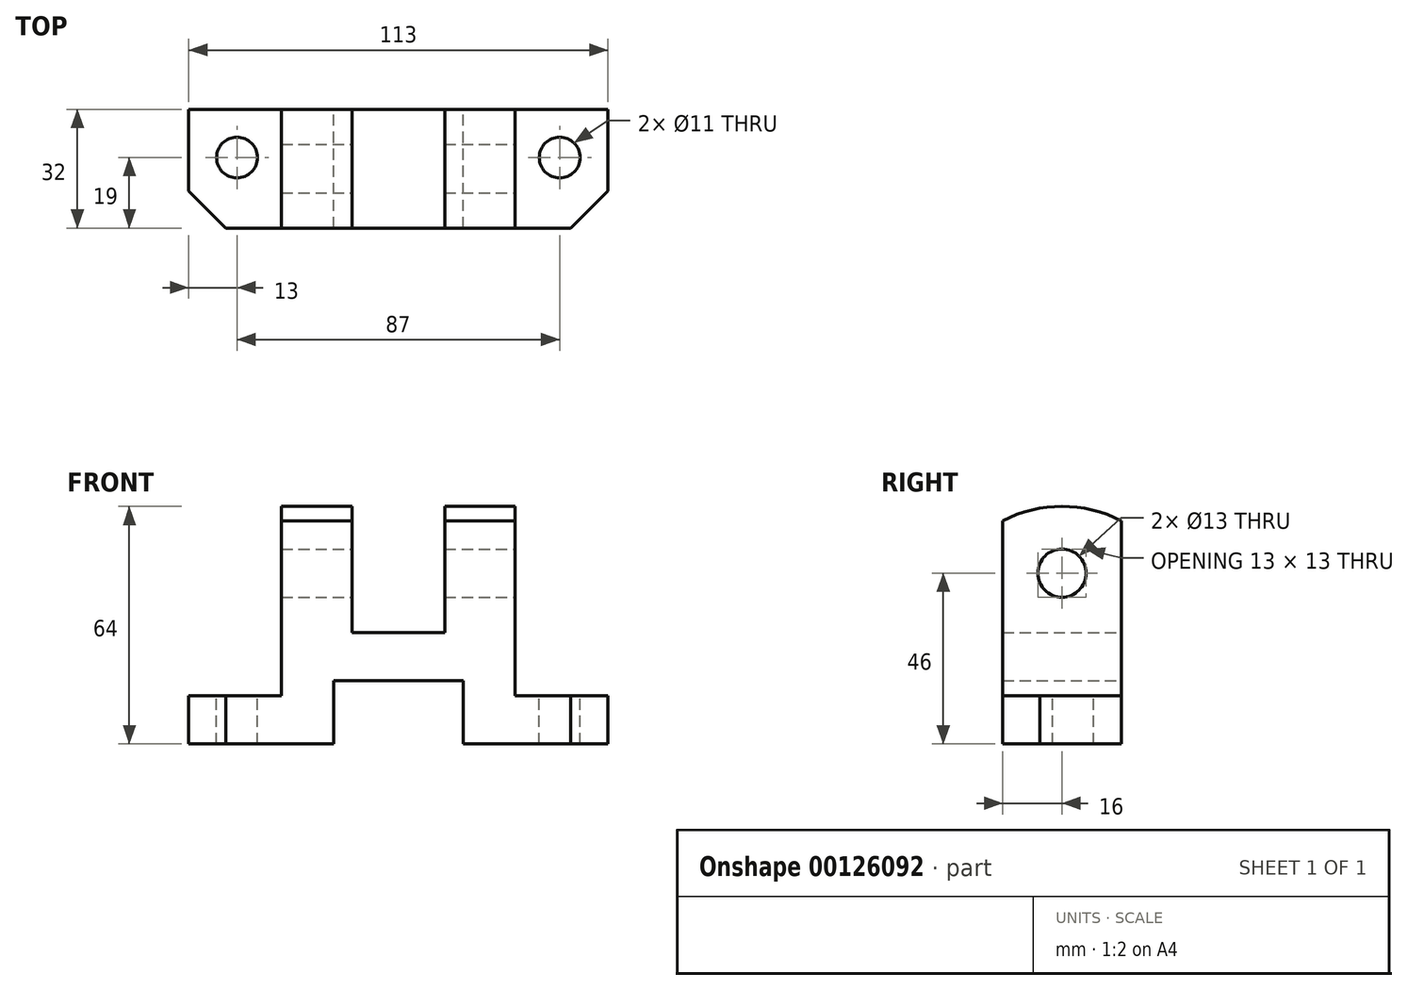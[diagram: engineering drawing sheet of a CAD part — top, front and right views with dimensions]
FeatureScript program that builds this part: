
annotation { "Feature Type Name" : "Feature", "Feature Type Description" : "" }
export const myFeature = defineFeature(function(context is Context, id is Id, definition is map)
    precondition{}
    {
        {
            var Q0;
            Q0=qCreatedBy(makeId("Front.planeOp"),FACE);
            var sketch = newSketch(context, id + "F0", { "sketchPlane" : qUnion([Q0])});
            skLineSegment(sketch, "E0", {"start": v(0, 0) * mm, "end": v(0, 17) * mm, "construction": true});
            skLineSegment(sketch, "E1", {"start": v(0, 17) * mm, "end": v(0, 30) * mm});
            skLineSegment(sketch, "E2", {"start": v(0, 30) * mm, "end": v(12.5, 30) * mm});
            skLineSegment(sketch, "E3", {"start": v(12.5, 30) * mm, "end": v(12.5, 64) * mm});
            skLineSegment(sketch, "E4", {"start": v(12.5, 64) * mm, "end": v(31.5, 64) * mm});
            skLineSegment(sketch, "E5", {"start": v(31.5, 64) * mm, "end": v(31.5, 13) * mm});
            skLineSegment(sketch, "E6", {"start": v(31.5, 13) * mm, "end": v(56.5, 13) * mm});
            skLineSegment(sketch, "E7", {"start": v(56.5, 13) * mm, "end": v(56.5, 0) * mm});
            skLineSegment(sketch, "E8", {"start": v(0, 17) * mm, "end": v(17.5, 17) * mm});
            skLineSegment(sketch, "E9", {"start": v(17.5, 17) * mm, "end": v(17.5, 0) * mm});
            skLineSegment(sketch, "E10", {"start": v(17.5, 0) * mm, "end": v(56.5, 0) * mm});
            skLineSegment(sketch, "E11.MirrorCS", {"start": v(-31.5, 64) * mm, "end": v(-31.5, 13) * mm});
            skLineSegment(sketch, "E12.MirrorCS", {"start": v(-12.5, 30) * mm, "end": v(-12.5, 64) * mm});
            skLineSegment(sketch, "E13.MirrorCS", {"start": v(0, 30) * mm, "end": v(-12.5, 30) * mm});
            skLineSegment(sketch, "E14.MirrorCS", {"start": v(0, 17) * mm, "end": v(-17.5, 17) * mm});
            skLineSegment(sketch, "E15.MirrorCS", {"start": v(-12.5, 64) * mm, "end": v(-31.5, 64) * mm});
            skLineSegment(sketch, "E16.MirrorCS", {"start": v(-17.5, 0) * mm, "end": v(-56.5, 0) * mm});
            skLineSegment(sketch, "E17.MirrorCS", {"start": v(-31.5, 13) * mm, "end": v(-56.5, 13) * mm});
            skLineSegment(sketch, "E18.MirrorCS", {"start": v(-56.5, 13) * mm, "end": v(-56.5, 0) * mm});
            skLineSegment(sketch, "E19", {"start": v(-17.5, 17) * mm, "end": v(-17.5, 0) * mm});
            skSolve(sketch);
        }
        {
            var Q0;
            Q0=makeQuery(id+"F0.imprint","IMPRINT",FACE,{"disambiguationData":[TD([[makeQuery(id+"F0.imprint","IMPRINT",EDGE,{"derivedFrom":sQuery(id+"F0.wireOp",EDGE,"E1")}),1.0]])]});
            var Q1;
            Q1=makeQuery(id+"F0.imprint","IMPRINT",FACE,{"disambiguationData":[TD([[makeQuery(id+"F0.imprint","IMPRINT",EDGE,{"derivedFrom":sQuery(id+"F0.wireOp",EDGE,"E1")}),-1.0]])]});
            extrude(context, id + "F1", {"entities" : qUnion([Q0, Q1]), "endBound" : BoundingType.SYMMETRIC, "depth" : 32 * mm});
        }
        {
            var Q0;
            Q0=makeQuery(id+"F1.opExtrude","CAP_EDGE",EDGE,{"disambiguationData":[OSD([sQuery(id+"F0.wireOp",EDGE,"E18.MirrorCS")])],"isStart":false});
            var Q1;
            Q1=makeQuery(id+"F1.opExtrude","CAP_EDGE",EDGE,{"disambiguationData":[OSD([sQuery(id+"F0.wireOp",EDGE,"E7")])],"isStart":false});
            chamfer(context, id + "F2", {"entities" : qUnion([Q0, Q1]), "width" : 10 * mm, "tangentPropagation" : true});
        }
        {
            var Q0;
            Q0=makeQuery(id+"F1.opExtrude","SWEPT_FACE",FACE,{"disambiguationData":[OSD([sQuery(id+"F0.wireOp",EDGE,"E6")])]});
            var sketch = newSketch(context, id + "F3", { "sketchPlane" : qUnion([Q0])});
            skLineSegment(sketch, "E20.bottom", {"start": v(56.5, 16) * mm, "end": v(43.5, 16) * mm});
            skLineSegment(sketch, "E20.top", {"start": v(56.5, 3) * mm, "end": v(43.5, 3) * mm, "construction": true});
            skLineSegment(sketch, "E20.left", {"start": v(56.5, 16) * mm, "end": v(56.5, 3) * mm});
            skLineSegment(sketch, "E20.right", {"start": v(43.5, 16) * mm, "end": v(43.5, 3) * mm, "construction": true});
            skCircle(sketch, "E21", {"center": v(43.5, 3) * mm, "radius": 5.5 * mm});
            skCircle(sketch, "E22.MirrorC", {"center": v(-43.5, 3) * mm, "radius": 5.5 * mm});
            skSolve(sketch);
        }
        {
            var Q0;
            Q0 = qSketchRegion(id + "F3", true);
            extrude(context, id + "F4", {"entities" : qUnion([Q0]), "operationType" : NewBodyOperationType.REMOVE, "endBound" : BoundingType.THROUGH_ALL, "oppositeDirection" : true, "depth" : 25 * mm});
        }
        {
            var Q0;
            Q0=makeQuery(id+"F1.opExtrude","SWEPT_FACE",FACE,{"disambiguationData":[OSD([sQuery(id+"F0.wireOp",EDGE,"E5")])]});
            var sketch = newSketch(context, id + "F5", { "sketchPlane" : qUnion([Q0])});
            skArc(sketch, "E23", {"start": v(16, 60.13) * mm, "mid": v(0, 64) * mm, "end": v(-16, 60.13) * mm});
            skLineSegment(sketch, "E24", {"start": v(0, 0) * mm, "end": v(0, 46) * mm, "construction": true});
            skPoint(sketch, "E24.endSnap0", {"position": v(0, 13) * mm});
            skCircle(sketch, "E25", {"center": v(0, 46) * mm, "radius": 6.5 * mm});
            skLineSegment(sketch, "E26.0.1", {"start": v(16, 64) * mm, "end": v(-16, 64) * mm});
            skLineSegment(sketch, "E26.0.3", {"start": v(-16, 64) * mm, "end": v(16, 64) * mm});
            skLineSegment(sketch, "E27.0", {"start": v(16, 64) * mm, "end": v(16, 13) * mm});
            skLineSegment(sketch, "E28.0", {"start": v(-16, 64) * mm, "end": v(-16, 13) * mm});
            skSolve(sketch);
        }
        {
            var Q0;
            {var subQ0=sQuery(id+"F5.wireOp",EDGE,"E28.0");var subQ1=sQuery(id+"F5.wireOp",EDGE,"E23");var subQ2=makeQuery(id+"F5.imprint","INTERSECT",VERTEX,{"derivedFrom":[subQ1,subQ0]});Q0=makeQuery(id+"F5.imprint","IMPRINT",FACE,{"disambiguationData":[TD([[makeQuery(id+"F5.imprint","IMPRINT",EDGE,{"disambiguationData":[TD([[subQ2,1.0]])],"derivedFrom":subQ1}),-1.0]])]});}
            var Q1;
            {var subQ0=sQuery(id+"F5.wireOp",EDGE,"E27.0");var subQ1=sQuery(id+"F5.wireOp",EDGE,"E23");var subQ2=makeQuery(id+"F5.imprint","INTERSECT",VERTEX,{"derivedFrom":[subQ1,subQ0]});Q1=makeQuery(id+"F5.imprint","IMPRINT",FACE,{"disambiguationData":[TD([[makeQuery(id+"F5.imprint","IMPRINT",EDGE,{"disambiguationData":[TD([[subQ2,-1.0]])],"derivedFrom":subQ1}),-1.0]])]});}
            var Q2;
            Q2=makeQuery(id+"F5.imprint","IMPRINT",FACE,{"disambiguationData":[TD([[makeQuery(id+"F5.imprint","IMPRINT",EDGE,{"derivedFrom":sQuery(id+"F5.wireOp",EDGE,"E25")}),1.0]])]});
            extrude(context, id + "F6", {"entities" : qUnion([Q0, Q1, Q2]), "operationType" : NewBodyOperationType.REMOVE, "endBound" : BoundingType.THROUGH_ALL, "oppositeDirection" : true, "depth" : 25 * mm});
        }
    });
